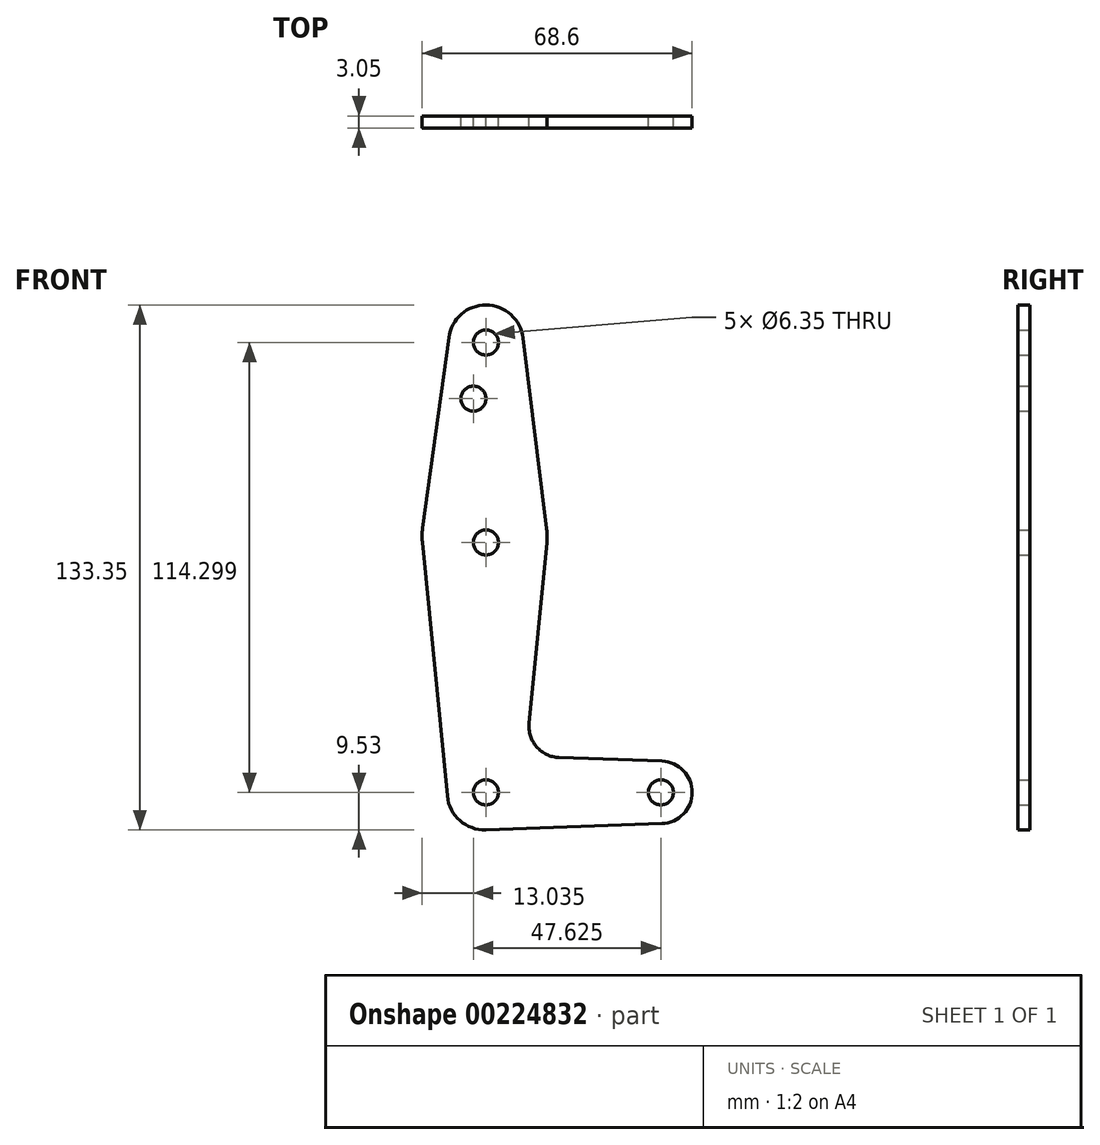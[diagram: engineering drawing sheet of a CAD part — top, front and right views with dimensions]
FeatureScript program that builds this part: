
annotation { "Feature Type Name" : "Feature", "Feature Type Description" : "" }
export const myFeature = defineFeature(function(context is Context, id is Id, definition is map)
    precondition{}
    {
        {
            var Q0;
            Q0=qCreatedBy(makeId("Front.planeOp"),FACE);
            var sketch = newSketch(context, id + "F0", { "sketchPlane" : qUnion([Q0])});
            skLineSegment(sketch, "E0", {"start": v(0, 61.73) * mm, "end": v(0, -63.5) * mm, "construction": true});
            skLineSegment(sketch, "E1", {"start": v(0, -63.5) * mm, "end": v(44.45, -63.5) * mm, "construction": true});
            skCircle(sketch, "E2", {"center": v(0, 50.8) * mm, "radius": 9.53 * mm});
            skCircle(sketch, "E3", {"center": v(-0.34, 1.55) * mm, "radius": 15.88 * mm});
            skCircle(sketch, "E4", {"center": v(-0.34, -63.5) * mm, "radius": 9.53 * mm});
            skCircle(sketch, "E5", {"center": v(44.45, -63.5) * mm, "radius": 7.94 * mm});
            skLineSegment(sketch, "E6", {"start": v(9.45, 51.96) * mm, "end": v(15.42, 3.49) * mm});
            skLineSegment(sketch, "E7", {"start": v(-9.44, 52.1) * mm, "end": v(-16.07, 3.7) * mm});
            skLineSegment(sketch, "E8", {"start": v(-16.14, 0) * mm, "end": v(-9.82, -64.43) * mm});
            skLineSegment(sketch, "E9", {"start": v(15.46, 0) * mm, "end": v(10.96, -45.92) * mm});
            skLineSegment(sketch, "E10", {"start": v(18.59, -54.64) * mm, "end": v(44.73, -55.57) * mm});
            skLineSegment(sketch, "E11", {"start": v(0, -73.02) * mm, "end": v(44.73, -71.43) * mm});
            skCircle(sketch, "E12", {"center": v(0, 50.8) * mm, "radius": 3.18 * mm});
            skCircle(sketch, "E13", {"center": v(0, 0) * mm, "radius": 3.18 * mm});
            skCircle(sketch, "E14", {"center": v(-3.17, 36.53) * mm, "radius": 3.18 * mm});
            skCircle(sketch, "E15", {"center": v(0, -63.5) * mm, "radius": 3.18 * mm});
            skCircle(sketch, "E16", {"center": v(44.45, -63.5) * mm, "radius": 3.18 * mm});
            skArc(sketch, "E17.filletArc", {"start": v(10.96, -45.92) * mm, "mid": v(12.89, -51.93) * mm, "end": v(18.59, -54.64) * mm});
            skSolve(sketch);
        }
        {
            var Q0;
            Q0 = qSketchRegion(id + "F0", true);
            extrude(context, id + "F1", {"entities" : qUnion([Q0]), "depth" : 3.05 * mm});
        }
    });
